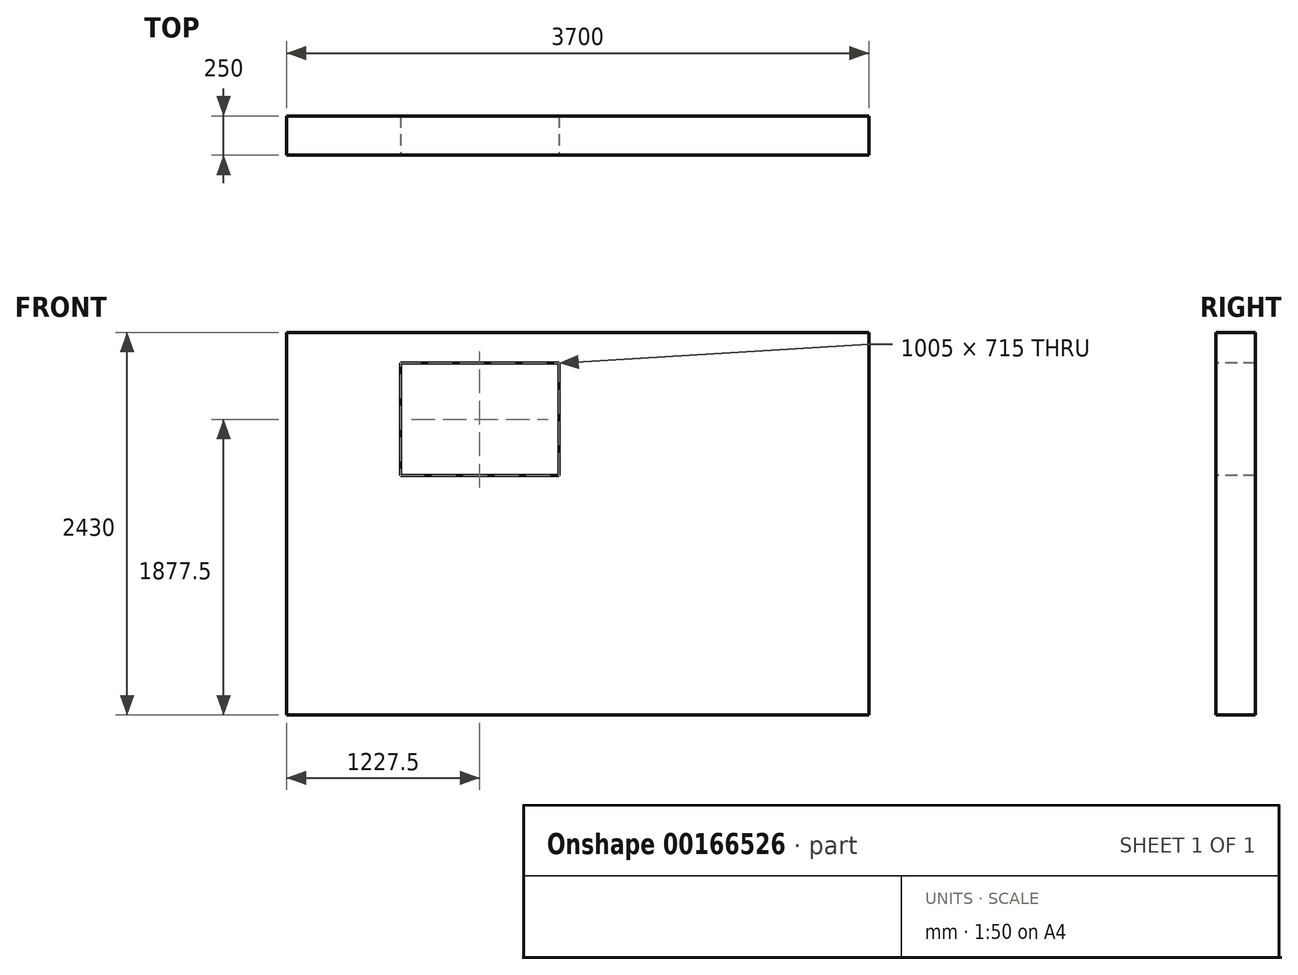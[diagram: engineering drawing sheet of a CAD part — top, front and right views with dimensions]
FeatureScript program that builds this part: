
annotation { "Feature Type Name" : "Feature", "Feature Type Description" : "" }
export const myFeature = defineFeature(function(context is Context, id is Id, definition is map)
    precondition{}
    {
        {
            var Q0;
            Q0=qCreatedBy(makeId("Front.planeOp"),FACE);
            var sketch = newSketch(context, id + "F0", { "sketchPlane" : qUnion([Q0])});
            skLineSegment(sketch, "E0.bottom", {"start": v(0, 0) * mm, "end": v(3700, 0) * mm});
            skLineSegment(sketch, "E0.top", {"start": v(0, 2430) * mm, "end": v(3700, 2430) * mm});
            skLineSegment(sketch, "E1", {"start": v(725, 1520) * mm, "end": v(0, 1520) * mm, "construction": true});
            skLineSegment(sketch, "E2", {"start": v(725, 1520) * mm, "end": v(725, 0) * mm, "construction": true});
            skLineSegment(sketch, "E3.bottom", {"start": v(725, 1520) * mm, "end": v(1730, 1520) * mm});
            skLineSegment(sketch, "E3.top", {"start": v(725, 2235) * mm, "end": v(1730, 2235) * mm});
            skLineSegment(sketch, "E3.left", {"start": v(725, 1520) * mm, "end": v(725, 2235) * mm});
            skLineSegment(sketch, "E3.right", {"start": v(1730, 1520) * mm, "end": v(1730, 2235) * mm});
            skLineSegment(sketch, "E4.bottom", {"start": v(3700, 0) * mm, "end": v(0, 0) * mm});
            skLineSegment(sketch, "E4.left", {"start": v(3700, 0) * mm, "end": v(3700, 85) * mm});
            skLineSegment(sketch, "E4.right", {"start": v(0, 0) * mm, "end": v(0, 85) * mm});
            skLineSegment(sketch, "E5", {"start": v(3700, 85) * mm, "end": v(3700, 2430) * mm});
            skLineSegment(sketch, "E6", {"start": v(0, 2430) * mm, "end": v(0, 85) * mm});
            skSolve(sketch);
        }
        {
            var Q0;
            Q0=makeQuery(id+"F0.imprint","IMPRINT",FACE,{"disambiguationData":[TD([[makeQuery(id+"F0.imprint","IMPRINT",EDGE,{"derivedFrom":sQuery(id+"F0.wireOp",EDGE,"E0.top")}),-1.0]])]});
            extrude(context, id + "F1", {"entities" : qUnion([Q0]), "oppositeDirection" : true, "depth" : 250 * mm});
        }
    });
